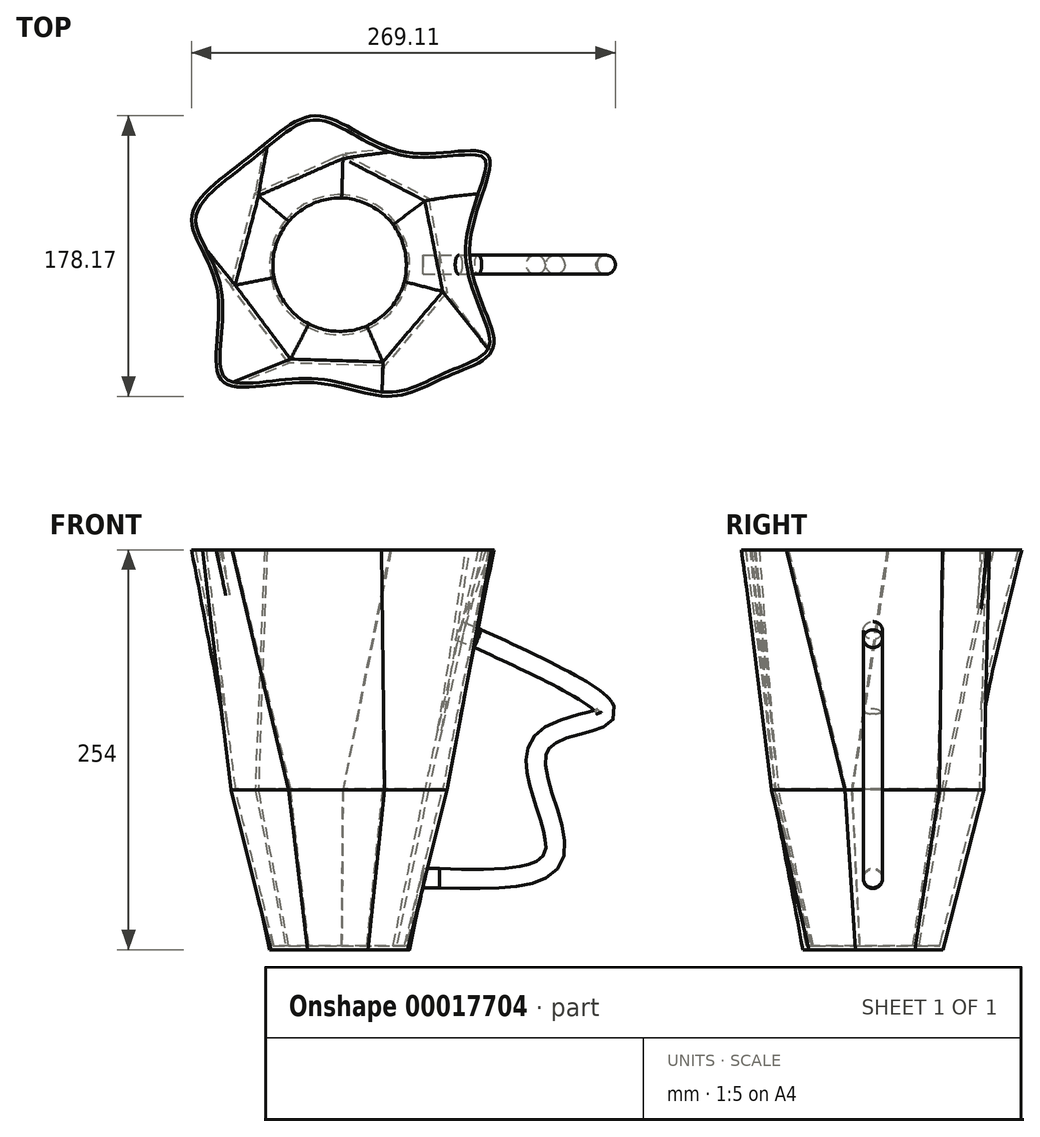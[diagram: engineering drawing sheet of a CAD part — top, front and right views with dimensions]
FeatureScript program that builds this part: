
annotation { "Feature Type Name" : "Feature", "Feature Type Description" : "" }
export const myFeature = defineFeature(function(context is Context, id is Id, definition is map)
    precondition{}
    {
        {
            var Q0;
            Q0=qCreatedBy(makeId("Top.planeOp"),FACE);
            var sketch = newSketch(context, id + "F0", { "sketchPlane" : qUnion([Q0])});
            skCircle(sketch, "E0", {"center": v(0, 0) * mm, "radius": 44.45 * mm});
            skSolve(sketch);
        }
        {
            var Q0;
            Q0=qCreatedBy(makeId("Top.planeOp"),FACE);
            cPlane(context, id + "F1", {"entities" : qUnion([Q0]), "cplaneType" : CPlaneType.OFFSET, "offset" : 101.6 * mm, "width" : 152.4 * mm, "height" : 152.4 * mm});
        }
        {
            var Q0;
            Q0=qCreatedBy(id+"F1.planeOp",FACE);
            var sketch = newSketch(context, id + "F2", { "sketchPlane" : qUnion([Q0])});
            skCircle(sketch, "E1.cCircle", {"center": v(0, 0) * mm, "radius": 63.42 * mm, "construction": true});
            skLineSegment(sketch, "E1.0", {"start": v(68.11, -17.76) * mm, "end": v(28.59, -64.32) * mm});
            skLineSegment(sketch, "E1.1", {"start": v(28.59, -64.32) * mm, "end": v(-32.47, -62.46) * mm});
            skLineSegment(sketch, "E1.2", {"start": v(-32.47, -62.46) * mm, "end": v(-69.07, -13.56) * mm});
            skLineSegment(sketch, "E1.3", {"start": v(-69.07, -13.56) * mm, "end": v(-53.67, 45.55) * mm});
            skLineSegment(sketch, "E1.4", {"start": v(-53.67, 45.55) * mm, "end": v(2.15, 70.36) * mm});
            skLineSegment(sketch, "E1.5", {"start": v(2.15, 70.36) * mm, "end": v(56.35, 42.18) * mm});
            skLineSegment(sketch, "E1.6", {"start": v(56.35, 42.18) * mm, "end": v(68.11, -17.76) * mm});
            skPoint(sketch, "E1.0.midPoint", {"position": v(48.35, -41.04) * mm});
            skSolve(sketch);
        }
        {
            var Q0;
            Q0=makeQuery(id+"F2.imprint","IMPRINT",FACE,{"disambiguationData":[TD([[makeQuery(id+"F2.imprint","IMPRINT",EDGE,{"derivedFrom":sQuery(id+"F2.wireOp",EDGE,"E1.0")}),-1.0]])]});
            var Q1;
            Q1=makeQuery(id+"F0.imprint","IMPRINT",FACE,{"disambiguationData":[TD([[makeQuery(id+"F0.imprint","IMPRINT",EDGE,{"derivedFrom":sQuery(id+"F0.wireOp",EDGE,"E0")}),1.0]])]});
            loft(context, id + "F3", {"sheetProfilesArray" : [{ "sheetProfileEntities" : qUnion([Q0]) }, { "sheetProfileEntities" : qUnion([Q1]) }]});
        }
        {
            var Q0;
            Q0=qCreatedBy(id+"F1.planeOp",FACE);
            cPlane(context, id + "F4", {"entities" : qUnion([Q0]), "cplaneType" : CPlaneType.OFFSET, "offset" : 152.4 * mm, "width" : 152.4 * mm, "height" : 152.4 * mm});
        }
        {
            var Q0;
            Q0=qCreatedBy(id+"F4.planeOp",FACE);
            var sketch = newSketch(context, id + "F5", { "sketchPlane" : qUnion([Q0])});
            skFitSpline(sketch, "E2", {"points": [v(69.95, -70.28) * mm, v(32.23, -83.58) * mm, v(-20.1, -74.77) * mm, v(-74.77, -73.6) * mm, v(-77.76, -15.78) * mm, v(-93.88, 30.74) * mm, v(-56.5, 69.29) * mm, v(-13.62, 94.54) * mm, v(41.87, 71.61) * mm, v(94.38, 69.29) * mm, v(82.58, 8.14) * mm, v(97.7, -52) * mm, v(69.95, -70.28) * mm]});
            skSolve(sketch);
        }
        {
            var Q1;
            Q1=makeQuery(id+"F5.imprint","IMPRINT",FACE,{"disambiguationData":[TD([[makeQuery(id+"F5.imprint","IMPRINT",EDGE,{"derivedFrom":sQuery(id+"F5.wireOp",EDGE,"E2")}),-1.0]])]});
            var Q2;
            Q2=makeQuery(id+"F3.opLoft","CAP_FACE",FACE,{"disambiguationData":[OSD([makeQuery(id+"F2.imprint","IMPRINT",FACE,{"disambiguationData":[TD([[makeQuery(id+"F2.imprint","IMPRINT",EDGE,{"derivedFrom":sQuery(id+"F2.wireOp",EDGE,"E1.0")}),-1.0]])]})])],"isStart":true});
            loft(context, id + "F6", {"operationType" : NewBodyOperationType.ADD, "sheetProfilesArray" : [{ "sheetProfileEntities" : qUnion([Q1]) }, { "sheetProfileEntities" : qUnion([Q2]) }]});
        }
        {
            var Q0;
            Q0=makeQuery(id+"F6.opLoft","CAP_FACE",FACE,{"disambiguationData":[OSD([makeQuery(id+"F5.imprint","IMPRINT",FACE,{"disambiguationData":[TD([[makeQuery(id+"F5.imprint","IMPRINT",EDGE,{"derivedFrom":sQuery(id+"F5.wireOp",EDGE,"E2")}),-1.0]])]})])],"isStart":true});
            shell(context, id + "F7", {"entities" : qUnion([Q0]), "thickness" : 2.54 * mm});
        }
        {
            var Q0;
            Q0=qCreatedBy(makeId("Right.planeOp"),FACE);
            cPlane(context, id + "F8", {"entities" : qUnion([Q0]), "cplaneType" : CPlaneType.OFFSET, "offset" : 63.5 * mm, "width" : 152.4 * mm, "height" : 152.4 * mm});
        }
        {
            var Q0;
            Q0=qCreatedBy(id+"F8.planeOp",FACE);
            var sketch = newSketch(context, id + "F9", { "sketchPlane" : qUnion([Q0])});
            skCircle(sketch, "E3", {"center": v(0, 45.42) * mm, "radius": 6.08 * mm});
            skSolve(sketch);
        }
        {
            var Q0;
            Q0=qCreatedBy(makeId("Front.planeOp"),FACE);
            var sketch = newSketch(context, id + "F10", { "sketchPlane" : qUnion([Q0])});
            skFitSpline(sketch, "E4", {"points": [v(63.75, 45.04) * mm, v(136.86, 60.96) * mm, v(127.11, 129.52) * mm, v(168.7, 149.01) * mm, v(87.8, 198.08) * mm], "startDerivative": vector(398.54, -12.53) * mm, "endDerivative": vector(-452.59, 208.66) * mm});
            skSolve(sketch);
        }
        {
            var Q0;
            Q0=makeQuery(id+"F9.imprint","IMPRINT",FACE,{"disambiguationData":[TD([[makeQuery(id+"F9.imprint","IMPRINT",EDGE,{"derivedFrom":sQuery(id+"F9.wireOp",EDGE,"E3")}),1.0]])]});
            var Q1;
            Q1=sQuery(id+"F10.wireOp",EDGE,"E4");
            sweep(context, id + "F11", {"profiles" : qUnion([Q0]), "path" : qUnion([Q1])});
        }
        {
            var Q0;
            Q0=makeQuery(id+"F11.opSweep","CAP_FACE",FACE,{"disambiguationData":[OSD([sQuery(id+"F9.wireOp",EDGE,"E3"),sQuery(id+"F10.wireOp",VERTEX,"E4.start")])],"isStart":true});
            extrude(context, id + "F12", {"entities" : qUnion([Q0]), "depth" : 10.4 * mm});
        }
        {
            var Q0;
            Q0=makeQuery(id+"F11.opSweep","CAP_FACE",FACE,{"disambiguationData":[OSD([sQuery(id+"F9.wireOp",EDGE,"E3"),sQuery(id+"F10.wireOp",VERTEX,"E4.end")])],"isStart":false});
            extrude(context, id + "F13", {"entities" : qUnion([Q0]), "depth" : 13.15 * mm});
        }
    });
